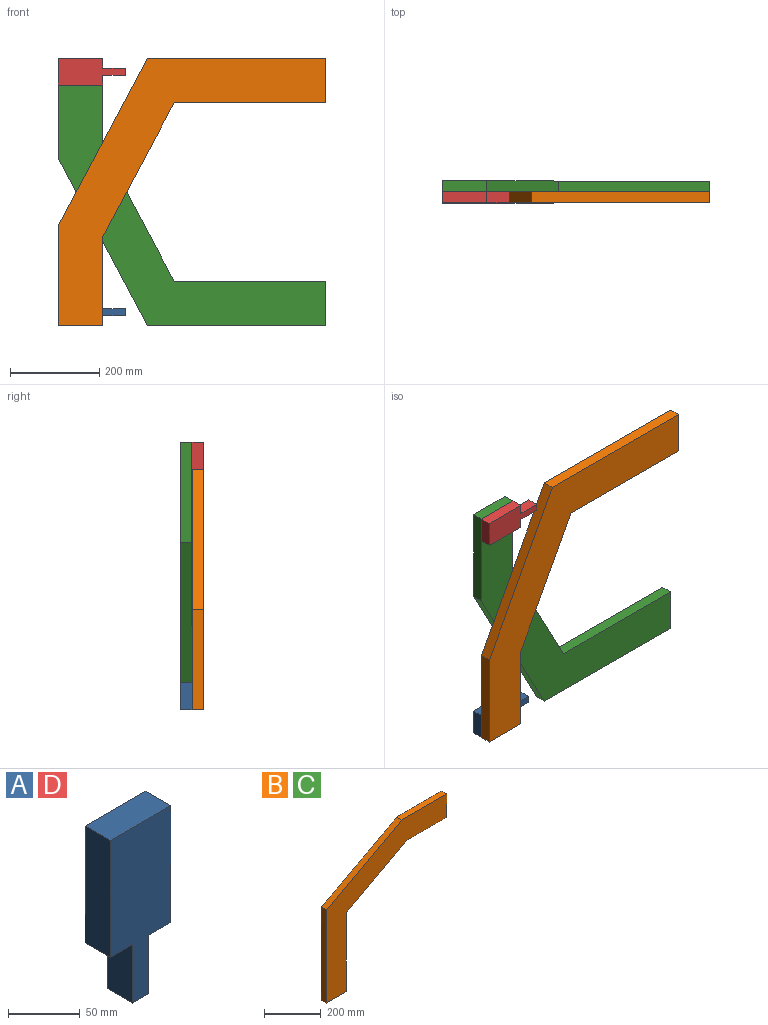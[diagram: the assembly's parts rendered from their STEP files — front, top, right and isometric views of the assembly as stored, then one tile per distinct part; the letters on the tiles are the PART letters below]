
ASSEMBLY  parts=4 mates=7
PART A: 10 faces, bbox 60x25x150 mm
  f0: plane 25x22mm, normal (0,0,-1), area 550mm2, adj f1,f7,f8,f9
  f1: plane 100x25mm, normal (1,0,0), area 2500mm2, adj f0,f2,f8,f9
  f2: plane 60x25mm, normal (0,0,1), area 1500mm2, adj f1,f3,f8,f9
  f3: plane 100x25mm, normal (-1,0,0), area 2500mm2, adj f2,f4,f8,f9
  f4: plane 25x22mm, normal (0,0,-1), area 550mm2, adj f3,f5,f8,f9
  f5: plane 50x25mm, normal (-1,0,0), area 1250mm2, adj f4,f6,f8,f9
  f6: plane 25x16mm, normal (0,0,-1), area 400mm2, adj f5,f7,f8,f9
  f7: plane 50x25mm, normal (1,0,0), area 1250mm2, adj f0,f6,f8,f9
  f8: plane 150x60mm, normal (0,-1,0), area 6800mm2, adj f0,f1,f2,f3,f4,f5,f6,f7
  f9: plane 150x60mm, normal (0,1,0), area 6800mm2, adj f0,f1,f2,f3,f4,f5,f6,f7
PART B: 10 faces, bbox 600x25x600 mm
  f0: plane 400x25mm, normal (-1,0,0), area 10000mm2, adj f1,f7,f8,f9
  f1: plane 100x25mm, normal (0,0,-1), area 2500mm2, adj f0,f2,f8,f9
  f2: plane 340x25mm, normal (1,0,0), area 8500mm2, adj f1,f3,f8,f9
  f3: plane 300x160mm, normal (0.47,0,-0.88), area 8500mm2, adj f2,f4,f8,f9
  f4: plane 200x25mm, normal (0,0,-1), area 5000mm2, adj f3,f5,f8,f9
  f5: plane 100x25mm, normal (1,0,0), area 2500mm2, adj f4,f6,f8,f9
  f6: plane 225x25mm, normal (0,0,1), area 5625mm2, adj f5,f7,f8,f9
  f7: plane 375x200mm, normal (-0.47,0,0.88), area 10625mm2, adj f0,f6,f8,f9
  f8: plane 600x600mm, normal (0,-1,0), area 96500mm2, adj f0,f1,f2,f3,f4,f5,f6,f7
  f9: plane 600x600mm, normal (0,1,0), area 96500mm2, adj f0,f1,f2,f3,f4,f5,f6,f7
PART C: same geometry as B
PART D: same geometry as A
PLACE A rot(axis=(0,-1,0),90deg) t=(455.19,-225.26,-279.07)mm
PLACE B rot(axis=(0.71,0,-0.71),180deg) t=(385.27,-275.26,-105.21)mm
PLACE C rot(axis=(0,-1,0),90deg) t=(385.27,-225.26,-155.81)mm
PLACE D rot(axis=(0,-1,0),90deg) t=(455.19,-250.26,260.93)mm
MATE fastened D.f2 <-> C.f6  axis (-1,0,0) through (295.19,-250.26,169.49)mm
MATE planar B.f5 <-> A.f3  axis (0,0,-1) through (345.19,-250.26,-430.51)mm
MATE planar B.f6 <-> C.f6  axis (-1,0,0) through (295.19,-262.76,-318.01)mm
MATE planar C.f8 <-> B.f8  axis (0,-1,0) through (725.19,-250.26,-330.51)mm
MATE planar B.f5 <-> C.f0  axis (0,0,-1) through (345.19,-275.26,-430.51)mm
MATE planar A.f2 <-> B.f6  axis (-1,0,0) through (295.19,-225.26,-400.51)mm
MATE planar A.f8 <-> B.f8  axis (0,-1,0) through (354.02,-250.26,-400.51)mm
